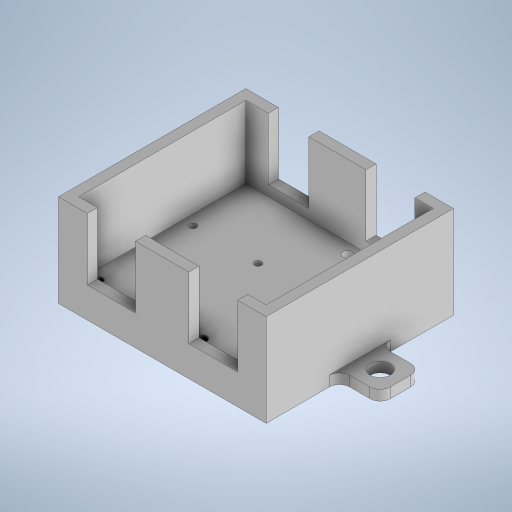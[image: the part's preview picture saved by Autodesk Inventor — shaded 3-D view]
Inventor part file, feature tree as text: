
AUTODESK INVENTOR PART (.ipt)
format: ipt  version: 2024 (Build 280153000, 153)  size: 599,552 bytes
history: native  units: in
note: dims shown in document units (in); Inventor stores cm internally (conversion verified against a paired STEP export)
features: projected_geometry x8, extrude x5, sketch x5, fillet x1
ambient origin geometry x8: Origin, YZ Plane, XZ Plane, XY Plane, X Axis, Y Axis, Z Axis, Center Point
bodies: Solid1 (feature_tree)
feature tree (19):
  extrude  "Extrusion1"  Depth=0.125in TaperAngle=0.0deg
  extrude  "Extrusion2"  Depth=0.125in
  extrude  "Extrusion3"  Depth=0.76in TaperAngle=0.0deg
  extrude  "Extrusion4"  Depth=0.125in
  sketch  "Sketch6"  dims[d9=0.125in d10=0.0in d11=0.22in]
  extrude  "Extrusion5"  Depth=0.125in
  fillet  "Fillet1"  Radius=0.11in
  sketch  "Sketch3"  dims[d0=0.25in d1=0.125in d2=0.0in]
  sketch  "Sketch4"  dims[d3=0.025in d4=0.125in]
  projected_geometry  "Projected Loop1"
  projected_geometry  "Projected Loop2"
  projected_geometry  "Projected Loop3"
  sketch  "Sketch5"  dims[d5=0.125in d6=0.0in d7=0.76in d8=0.0in]
  projected_geometry  "Projected Loop4"
  projected_geometry  "Projected Loop5"
  projected_geometry  "Projected Loop6"
  projected_geometry  "Projected Loop7"
  sketch  "Sketch7"  dims[d12=0.22in d13=0.22in d14=0.11in d15=0.22in d16=0.125in d17=0.5in d18=0.25in d19=0.5in d20=0.5in d21=0.5in d22=0.25in d23=0.25in d24=0.125in d25=0.125in d26=0.0in d27=0.125in]
  projected_geometry  "Projected Loop8"
